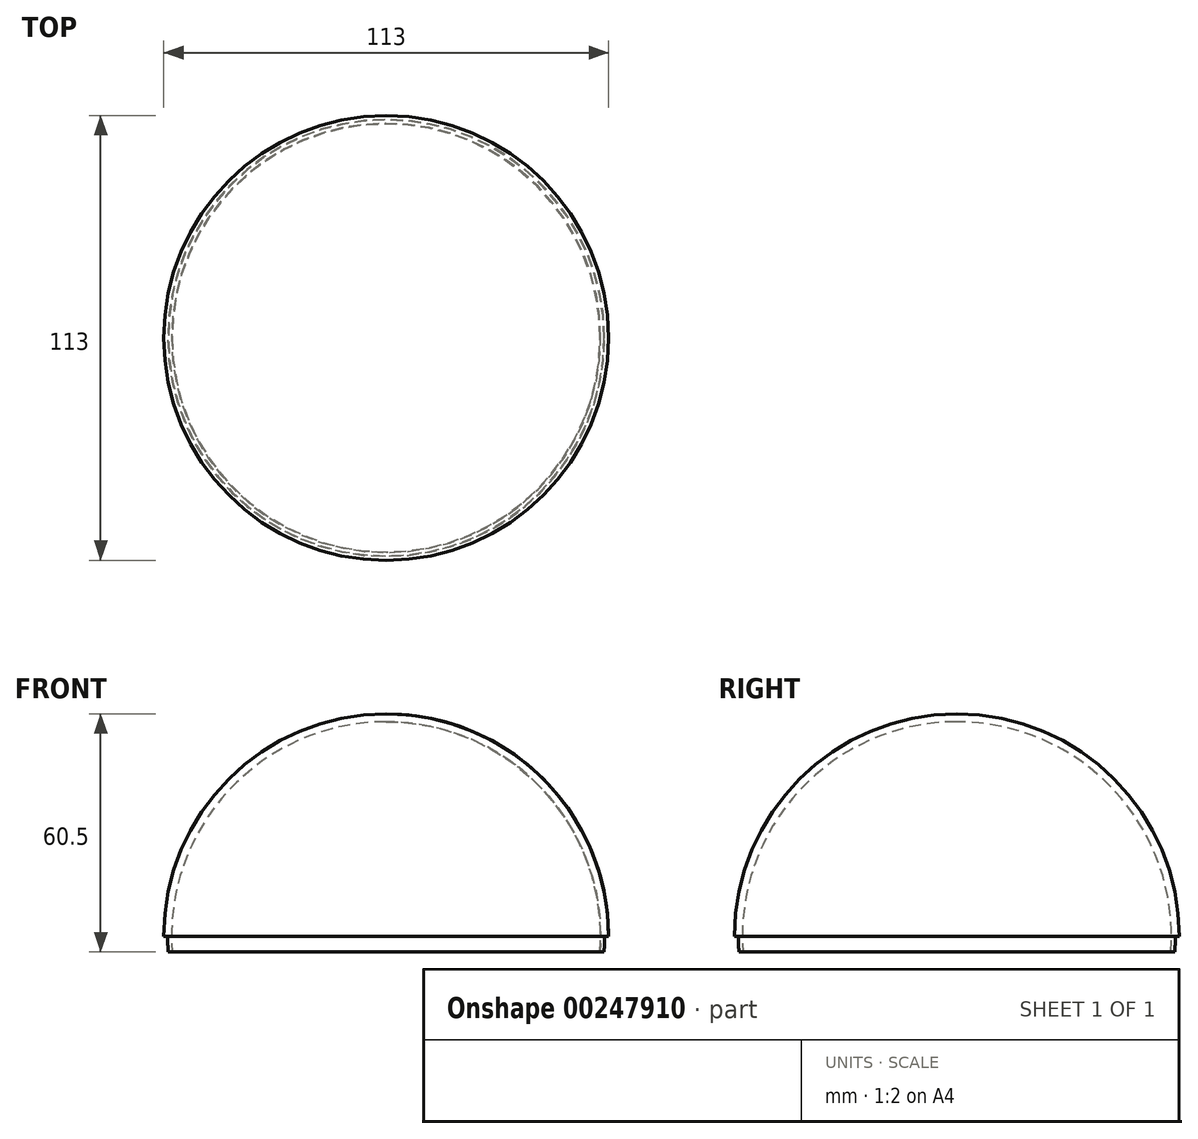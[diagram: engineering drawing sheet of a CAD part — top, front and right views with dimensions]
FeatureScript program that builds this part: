
annotation { "Feature Type Name" : "Feature", "Feature Type Description" : "" }
export const myFeature = defineFeature(function(context is Context, id is Id, definition is map)
    precondition{}
    {
        {
            var Q0;
            Q0=qCreatedBy(makeId("Front.planeOp"),FACE);
            var sketch = newSketch(context, id + "F0", { "sketchPlane" : qUnion([Q0])});
            skLineSegment(sketch, "E0", {"start": v(0, 0) * mm, "end": v(0, 56.5) * mm});
            skArc(sketch, "E1", {"start": v(56.5, 0) * mm, "mid": v(39.95, 39.95) * mm, "end": v(0, 56.5) * mm});
            skArc(sketch, "E2", {"start": v(55.36, -4) * mm, "mid": v(40.63, 37.8) * mm, "end": v(0, 55.5) * mm});
            skLineSegment(sketch, "E3", {"start": v(0, 0) * mm, "end": v(56.5, 0) * mm});
            skArc(sketch, "E4", {"start": v(54.35, -4) * mm, "mid": v(39.93, 37.1) * mm, "end": v(0, 54.5) * mm});
            skLineSegment(sketch, "E5.trimOffspring", {"start": v(55.36, -4) * mm, "end": v(54.35, -4) * mm});
            skSolve(sketch);
        }
        {
            var Q0;
            {var subQ0=sQuery(id+"F0.wireOp",EDGE,"E2");var subQ1=sQuery(id+"F0.wireOp",EDGE,"E0");var subQ2=makeQuery(id+"F0.imprint","INTERSECT",VERTEX,{"derivedFrom":[subQ1,subQ0]});Q0=makeQuery(id+"F0.imprint","IMPRINT",FACE,{"disambiguationData":[TD([[makeQuery(id+"F0.imprint","IMPRINT",EDGE,{"disambiguationData":[TD([[subQ2,1.0]])],"derivedFrom":subQ1}),-1.0]])]});}
            var Q1;
            {var subQ0=sQuery(id+"F0.wireOp",EDGE,"E1");Q1=makeQuery(id+"F0.imprint","IMPRINT",FACE,{"disambiguationData":[TD([[makeQuery(id+"F0.imprint","IMPRINT",EDGE,{"derivedFrom":subQ0}),1.0]])]});}
            var Q2;
            {var subQ0=sQuery(id+"F0.wireOp",EDGE,"E5.trimOffspring");Q2=makeQuery(id+"F0.imprint","IMPRINT",FACE,{"disambiguationData":[TD([[makeQuery(id+"F0.imprint","IMPRINT",EDGE,{"derivedFrom":subQ0}),-1.0]])]});}
            var Q3;
            Q3=sQuery(id+"F0.wireOp",EDGE,"E0");
            revolve(context, id + "F1", {"entities" : qUnion([Q0, Q1, Q2]), "axis" : qUnion([Q3]), "revolveType" : RevolveType.FULL});
        }
    });
